# Revit family: QF_Moffat_INB8200R5-B_Induction_Cooktop_cat
name_source: partatom
category: Specialty Equipment
units: mm (PartAtom-declared; Revit-internal decimal feet)

## family parameters
Always vertical = Yes
Cut with Voids When Loaded = No
Part Type = Normal
Room Calculation Point = No
Round Connector Dimension = Use Diameter
Shared = No
Work Plane-Based = No

## types (1)
- QF_Moffat_INB8200R5-B_Induction_Cooktop_cat
    Apparent Power = 10051 VA
    Conn Conduit = Yes
    Cycle = 60 Hz
    Depth = 805 mm
    Description = Induction Cooktop
    Elec Conn Connection Height = 0 mm  [stored 0 ft]
    Elec Conn RI Height = 0 mm  [stored 0 ft]
    FL Amps = 14 A
    Foodservice Equipment Identifier = Yes
    Height = 570 mm  [stored 1.87008 ft]
    Identify Quantity as Lot = Yes
    Length = 450 mm  [stored 1.47638 ft]
    Manufacturer = Moffat
    Max Overcurrent Protection = 0 A
    Min Ckt Ampacity = 0 A
    Model = INB8200R5-B
    Number of Poles = 1
    Phase = 3
    Volts = 415 V
    Watts = 10000 W
    Weight in Kilograms = 88

note: [stored X ft] marks values corroborated as IEEE doubles in the binary element streams (Revit-internal decimal feet)

## geometry (parser evidence)
native form markers: Sweep x6
no freeform markers — native parametric forms only
